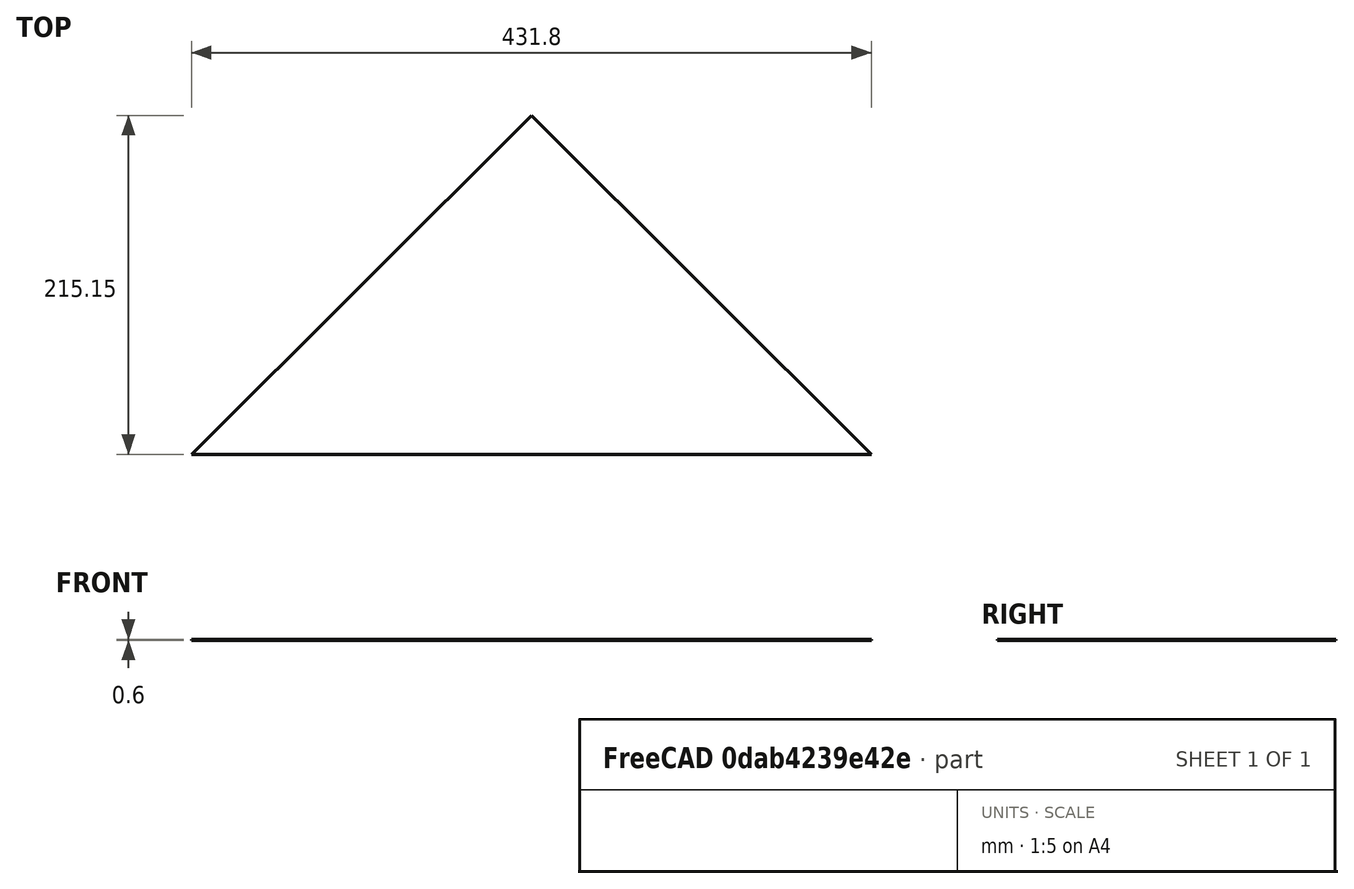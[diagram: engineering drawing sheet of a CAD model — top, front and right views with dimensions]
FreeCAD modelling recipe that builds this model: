
FCSTD DOCUMENT  (FreeCAD 0.19R22411 (Git))
Label: body
License: All rights reserved
LicenseURL: http://en.wikipedia.org/wiki/All_rights_reserved
objects: Sketcher::SketchObject×1, PartDesign::Pad×1, PartDesign::Body×1
note: 4 computed .brp shape members not serialized (recipe doc carries the construction recipe); baked Part::Feature solids carry a one-line shape summary decoded from their .brp

FEATURE [Sketcher::SketchObject] Sketch
  MapMode = 5
  Support = -> [XY_Plane]
  sketch-geometry (4):
    g0: LineSegment StartX=-215.9 StartY=0 StartZ=0 EndX=-7.3044e-12 EndY=215.152 EndZ=0
    g1: LineSegment StartX=-7.3044e-12 StartY=215.152 StartZ=0 EndX=215.9 EndY=0 EndZ=0
    g2: LineSegment StartX=215.9 StartY=0 StartZ=0 EndX=0 EndY=0 EndZ=0
    g3: LineSegment StartX=-215.9 StartY=0 StartZ=0 EndX=0 EndY=0 EndZ=0
  constraints (11):
    c: Horizontal(g2)
    c: Horizontal(g3)
    c: Equal(g0,g1)
    c: Coincident(g0,g3)
    c: Coincident(g3,g-1)
    c: Equal(g3,g2)
    c: Coincident(g0,g1)
    c: Coincident(g1,g2)
    c: Coincident(g2,g3)
    c: DistanceX(g0,g1) = 431.8
    c: Distance(g0,g1) = 304.8
FEATURE [PartDesign::Pad] Pad
  AllowMultiFace = false
  Length = 0.6
  Length2 = 100
  Profile = -> Sketch
  Type = 0
FEATURE [PartDesign::Body] Body
  Group = -> [Sketch,Pad]
  Origin = -> Origin
  Tip = -> Pad
